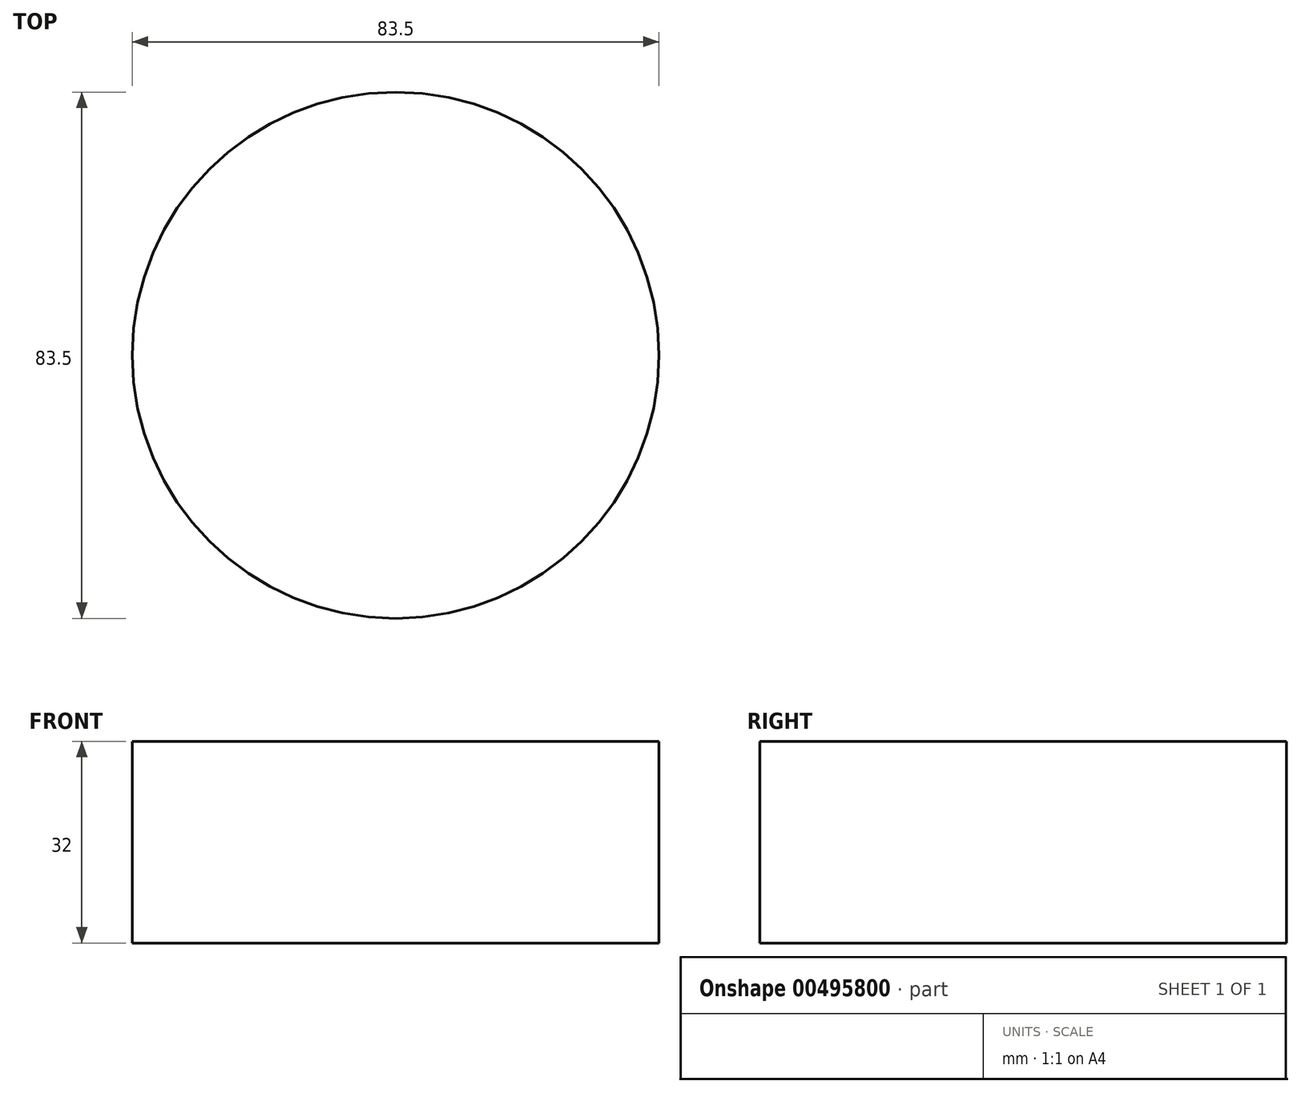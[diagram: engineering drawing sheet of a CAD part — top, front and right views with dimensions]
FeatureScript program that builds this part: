
annotation { "Feature Type Name" : "Feature", "Feature Type Description" : "" }
export const myFeature = defineFeature(function(context is Context, id is Id, definition is map)
    precondition{}
    {
        {
            var Q0;
            Q0=qCreatedBy(makeId("Top.planeOp"),FACE);
            var sketch = newSketch(context, id + "F0", { "sketchPlane" : qUnion([Q0])});
            skCircle(sketch, "E0", {"center": v(0, 0) * mm, "radius": 41.75 * mm});
            skSolve(sketch);
        }
        {
            var Q0;
            Q0 = qSketchRegion(id + "F0", true);
            extrude(context, id + "F1", {"entities" : qUnion([Q0]), "depth" : 32 * mm});
        }
        {
            var Q0;
            Q0=qCreatedBy(makeId("Front.planeOp"),FACE);
            var sketch = newSketch(context, id + "F2", { "sketchPlane" : qUnion([Q0])});
            skLineSegment(sketch, "E1", {"start": v(-35.75, 0) * mm, "end": v(0, 30) * mm});
            skLineSegment(sketch, "E2", {"start": v(0, 30) * mm, "end": v(35.75, 0) * mm});
            skLineSegment(sketch, "E3", {"start": v(-17.88, 15) * mm, "end": v(17.88, 15) * mm});
            skLineSegment(sketch, "E4", {"start": v(0, 30) * mm, "end": v(0, 0) * mm, "construction": true});
            skLineSegment(sketch, "E5", {"start": v(-35.75, 0) * mm, "end": v(-96.39, -10.7) * mm});
            skLineSegment(sketch, "E6", {"start": v(35.75, 0) * mm, "end": v(93.61, -21.06) * mm});
            skSolve(sketch);
        }
        {
            var Q0;
            Q0=makeQuery(id+"F1.opExtrude","SWEPT_BODY",BODY,{"disambiguationData":[OSD([sQuery(id+"F0.wireOp",EDGE,"E0")])]});
            var Q1;
            Q1=sQuery(id+"F2.wireOp",VERTEX,"E4.end");
            var Q2;
            Q2=sQuery(id+"F2.wireOp",VERTEX,"E4.start");
            transform(context, id + "F3", {"entities" : qUnion([Q0]), "transformType" : TransformType.TRANSLATION_ENTITY, "oppositeDirectionEntity" : false, "transformLine" : qUnion([Q1, Q2]), "makeCopy" : false});
        }
        {
            var Q0;
            Q0=sQuery(id+"F2.wireOp",EDGE,"E5");
            var Q1;
            Q1=sQuery(id+"F2.wireOp",EDGE,"E1");
            var Q2;
            Q2=sQuery(id+"F2.wireOp",EDGE,"E4");
            revolve(context, id + "F4", {"bodyType" : ToolBodyType.SURFACE, "surfaceEntities" : qUnion([Q0, Q1]), "axis" : qUnion([Q2]), "revolveType" : RevolveType.FULL});
        }
        {
            var Q0;
            Q0=makeQuery(id+"F4.opRevolve","SWEPT_EDGE",EDGE,{"disambiguationData":[OSD([sQuery(id+"F2.wireOp",VERTEX,"E1.start")])]});
            fillet(context, id + "F5", {"entities" : qUnion([Q0]), "radius" : 80 * mm, "tangentPropagation" : true, "allowEdgeOverflow" : false});
        }
    });
